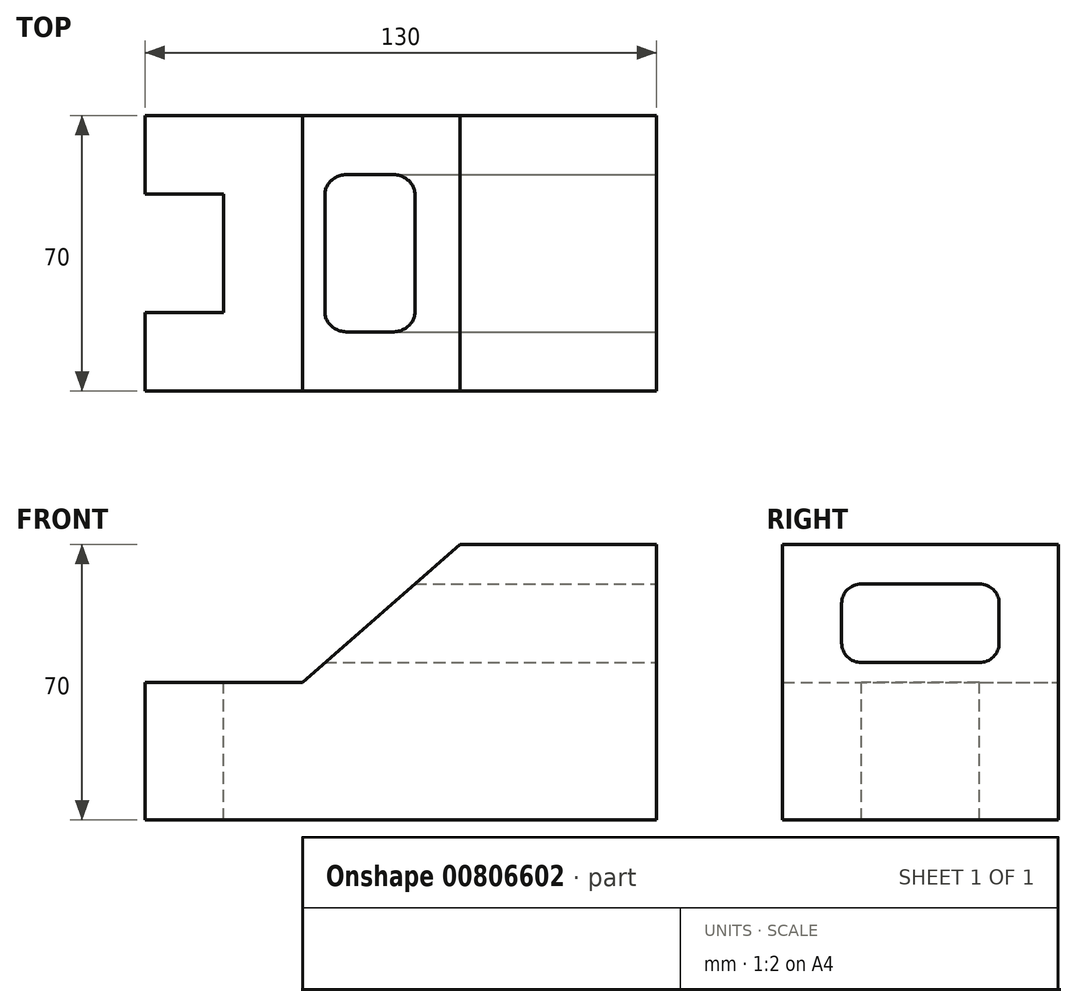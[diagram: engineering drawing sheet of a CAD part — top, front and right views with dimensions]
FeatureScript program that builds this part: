
annotation { "Feature Type Name" : "Feature", "Feature Type Description" : "" }
export const myFeature = defineFeature(function(context is Context, id is Id, definition is map)
    precondition{}
    {
        {
            var Q0;
            Q0=qCreatedBy(makeId("Front.planeOp"),FACE);
            var sketch = newSketch(context, id + "F0", { "sketchPlane" : qUnion([Q0])});
            skLineSegment(sketch, "E0.bottom", {"start": v(-65, -35) * mm, "end": v(65, -35) * mm});
            skLineSegment(sketch, "E0.top", {"start": v(15, 35) * mm, "end": v(65, 35) * mm});
            skLineSegment(sketch, "E0.left", {"start": v(-65, -35) * mm, "end": v(-65, 0) * mm});
            skLineSegment(sketch, "E0.right", {"start": v(65, -35) * mm, "end": v(65, 35) * mm});
            skPoint(sketch, "E0.middle", {"position": v(0, 0) * mm});
            skPoint(sketch, "E1.end.orphan", {"position": v(-65, 0) * mm});
            skPoint(sketch, "E1.start.orphan", {"position": v(0, 35) * mm});
            skLineSegment(sketch, "E2", {"start": v(15, 35) * mm, "end": v(-25, 0) * mm});
            skLineSegment(sketch, "E3", {"start": v(-25, 0) * mm, "end": v(-65, 0) * mm});
            skPoint(sketch, "E4.orphan", {"position": v(-65, 35) * mm});
            skSolve(sketch);
        }
        {
            var Q0;
            Q0 = qSketchRegion(id + "F0", true);
            extrude(context, id + "F1", {"entities" : qUnion([Q0]), "depth" : 70 * mm, "offsetDistance" : 25 * mm});
        }
        {
            var Q0;
            Q0=makeQuery(id+"F1.opExtrude","SWEPT_FACE",FACE,{"disambiguationData":[OSD([sQuery(id+"F0.wireOp",EDGE,"E3")])]});
            var sketch = newSketch(context, id + "F2", { "sketchPlane" : qUnion([Q0])});
            skLineSegment(sketch, "E5", {"start": v(-65, -20) * mm, "end": v(-45, -20) * mm});
            skPoint(sketch, "E5.endSnap0", {"position": v(-45, 0) * mm});
            skLineSegment(sketch, "E6", {"start": v(-45, -20) * mm, "end": v(-45, -50) * mm});
            skLineSegment(sketch, "E7", {"start": v(-45, -50) * mm, "end": v(-65, -50) * mm});
            skLineSegment(sketch, "E8", {"start": v(-65, -50) * mm, "end": v(-45, -50) * mm});
            skLineSegment(sketch, "E9", {"start": v(-65, -20) * mm, "end": v(-65, -50) * mm});
            skSolve(sketch);
        }
        {
            var Q0;
            Q0 = qSketchRegion(id + "F2", true);
            extrude(context, id + "F3", {"entities" : qUnion([Q0]), "operationType" : NewBodyOperationType.REMOVE, "endBound" : BoundingType.THROUGH_ALL, "oppositeDirection" : true, "depth" : 25 * mm, "offsetDistance" : 25 * mm});
        }
        {
            var Q0;
            Q0=makeQuery(id+"F1.opExtrude","SWEPT_FACE",FACE,{"disambiguationData":[OSD([sQuery(id+"F0.wireOp",EDGE,"E0.right")])]});
            var sketch = newSketch(context, id + "F4", { "sketchPlane" : qUnion([Q0])});
            skLineSegment(sketch, "E10.bottom", {"start": v(-50, 5) * mm, "end": v(-20, 5) * mm});
            skLineSegment(sketch, "E10.top", {"start": v(-50, 25) * mm, "end": v(-20, 25) * mm});
            skLineSegment(sketch, "E10.left", {"start": v(-55, 10) * mm, "end": v(-55, 20) * mm});
            skLineSegment(sketch, "E10.right", {"start": v(-15, 10) * mm, "end": v(-15, 20) * mm});
            skPoint(sketch, "E10.middle", {"position": v(-35, 15) * mm});
            skPoint(sketch, "E10.middle.positionSnap0", {"position": v(-35, 35) * mm});
            skPoint(sketch, "E10.centerSnap0", {"position": v(-35, 35) * mm});
            skPoint(sketch, "E11.visualSharp", {"position": v(-55, 25) * mm});
            skArc(sketch, "E11.filletArc", {"start": v(-50, 25) * mm, "mid": v(-53.54, 23.54) * mm, "end": v(-55, 20) * mm});
            skPoint(sketch, "E12.visualSharp", {"position": v(-55, 5) * mm});
            skArc(sketch, "E12.filletArc", {"start": v(-55, 10) * mm, "mid": v(-53.54, 6.46) * mm, "end": v(-50, 5) * mm});
            skPoint(sketch, "E13.visualSharp", {"position": v(-15, 25) * mm});
            skArc(sketch, "E13.filletArc", {"start": v(-15, 20) * mm, "mid": v(-16.46, 23.54) * mm, "end": v(-20, 25) * mm});
            skPoint(sketch, "E14.visualSharp", {"position": v(-15, 5) * mm});
            skArc(sketch, "E14.filletArc", {"start": v(-20, 5) * mm, "mid": v(-16.46, 6.46) * mm, "end": v(-15, 10) * mm});
            skSolve(sketch);
        }
        {
            var Q0;
            Q0=makeQuery(id+"F4.imprint","IMPRINT",FACE,{"disambiguationData":[TD([[makeQuery(id+"F4.imprint","IMPRINT",EDGE,{"derivedFrom":sQuery(id+"F4.wireOp",EDGE,"E10.bottom")}),1.0]])]});
            extrude(context, id + "F5", {"entities" : qUnion([Q0]), "operationType" : NewBodyOperationType.REMOVE, "endBound" : BoundingType.THROUGH_ALL, "oppositeDirection" : true, "depth" : 25 * mm, "offsetDistance" : 25 * mm});
        }
    });
